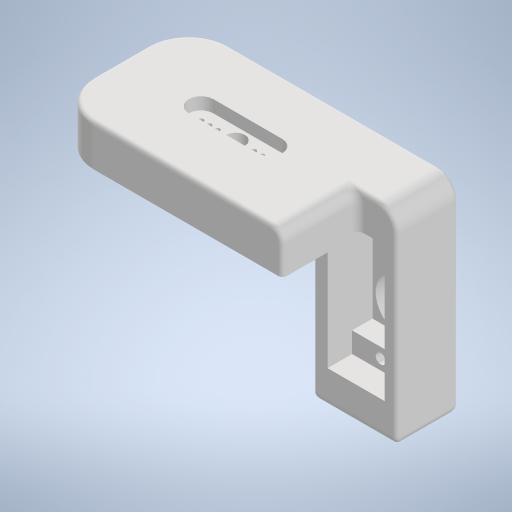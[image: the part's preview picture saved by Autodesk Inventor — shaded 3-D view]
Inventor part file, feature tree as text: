
AUTODESK INVENTOR PART (.ipt)
format: ipt  version: 2024 (Build 280153000, 153)  size: 644,608 bytes
history: native  units: mm
features: fillet x9, extrude x7, sketch x7, projected_geometry x6, other x4, plane x1, reference x1
ambient origin geometry x8: Origin, YZ Plane, XZ Plane, XY Plane, X Axis, Y Axis, Z Axis, Center Point
bodies: Solid1 (feature_tree)
feature tree (35):
  plane  "Work Plane1"
  extrude  "Extrusion1"  Depth=10.0mm
  fillet  "Fillet1"  Radius=10.0mm
  extrude  "Extrusion2"  Depth=10.0mm
  extrude  "Extrusion3"  Depth=20.0mm
  extrude  "Extrusion4"  Depth=40.0mm
  extrude  "Extrusion5"  Depth=14.0mm
  extrude  "Extrusion6"  Depth=10.0mm
  fillet  "Fillet2"  Radius=10.0mm
  fillet  "Fillet3"  Radius=11.0mm
  fillet  "Fillet4"  Radius=12.5mm
  fillet  "Fillet5"  Radius=6.5mm
  fillet  "Fillet6"  Radius=6.0mm
  extrude  "Extrusion8"  Depth=5.0mm
  fillet  "Fillet7"  Radius=5.0mm
  fillet  "Fillet8"  Radius=2.5mm
  fillet  "Fillet9"  Radius=2.5mm
  sketch  "Sketch1"  dims[d0=56.0mm d1=33.0mm d2=10.0mm d3=0.0mm]
  reference  "Reference1"
  sketch  "Sketch5"  dims[d4=10.0mm d9=10.0mm]
  projected_geometry  "Projected Loop1"
  sketch  "Sketch7"  dims[d10=50.0mm d11=20.0mm]
  sketch  "Sketch8"  dims[d12=18.0mm d13=40.0mm]
  projected_geometry  "Projected Loop2"
  sketch  "Sketch9"  dims[d14=15.0mm d15=0.0mm d16=14.0mm]
  projected_geometry  "Projected Loop3"
  projected_geometry  "Projected Loop4"
  sketch  "Sketch10"  dims[d17=23.0mm d18=25.0mm d19=10.0mm d20=11.0mm d21=0.0mm d22=12.5mm d23=6.5mm d24=6.0mm]
  projected_geometry  "Projected Loop5"
  projected_geometry  "Projected Loop6"
  sketch  "Sketch12"  dims[d25=11.0mm d26=0.0mm d27=5.0mm d28=5.0mm d29=2.5mm d30=2.5mm d31=28.0mm d32=7.0mm d33=7.0mm d34=19.5mm d35=6.0mm d36=0.0mm d37=2.5mm d38=2.5mm d39=28.0mm d40=7.0mm d41=25.5mm d42=25.5mm d43=5.0mm d44=0.0mm d45=5.0mm d46=3.0mm d47=1.0mm d48=1.0mm d49=2.0mm d58=6.0mm d59=6.0mm d60=3.0mm d61=0.0mm d62=5.0mm d63=2.0mm d64=2.0mm d53=0.5mm d54=0.872665mm d55=0.5mm d56=0.872665mm]
  other  "<userpath> windows\Documents\Inventor\Robotska_roka\Assembly4.iam"
  other  "Assembly4.iam"
  other  "SG90 - Micro Servo 9g - Tower Pro:2"
  other  "SG90 - Micro Servo 9g - Tower Pro.3"
